# Revit family: equip-water-cooler-hlsy-tylr-oval2-ebp
name_source: partatom
category: Plumbing Fixtures
units: mm (PartAtom-declared; Revit-internal decimal feet)

## family parameters
Always vertical = Yes
Cut with Voids When Loaded = No
OmniClass Number = 23.45.00.00
OmniClass Title = Sanitary, Laundry, and Cleaning Equipment
Part Type = Normal
Room Calculation Point = No
Round Connector Dimension = Use Diameter
Shared = No
Work Plane-Based = No

## types (5) — shared parameters
Activation = Curved Pushbars
Apparent Load Phase 1 = 0 VA
Back Panel = Yes
Bubbler = Double Bubbler
CW Connection = Yes
Chiller Option = No
Cooler Depth = 1' - 6"
Cooler Width = 1' - 7 3/4"
Description = Water Cooler
Filter = **ACC (HWF172)
HW Connection = No
Left Hand Unit = No
Manufacturer = halseytaylor
Model = OVL-II EBP FTN
Mounting Plate = Incl Suface Mtg Plate
Number of Poles = 1
Right Hand Unit = Yes
Rim Height = 2' - 10"
Sanitary Service Size Radius = 0' - 0"
Specification URL = http://www.halseytaylor.com
Type = Single-Extended
URL = http://www.halseytaylor.com
Vent Connection = No
Version = 1.0.0.0
Voltage = 0 V
Volts/Hertz = 115V/60Hz
Waste Connection = Yes
Water Service Flow = 0 GPM
Water Service Flow Out = 0 GPM
Water Service Radius = 0' - 0"
Water Service Size Radius = 0' - 0 1/4"
zero-valued in all types: Power Factor

## per-type parameters (varying)
| type | Basin Material | Body Material | Bubbler Material | Freeze Resistant | Panel Material | Wall Plate Material |
| OVL-II EBP FTN SS | Metal - Steel - Stainless - Chrome | Metal - Steel - Stainless - Color 1 | Metal - Steel - Stainless - Chrome | See 7634008683 | Metal - Steel - Stainless - Chrome | Metal - Steel - Stainless - Chrome |
| OVL-II EBP FTN AG | Metal - Steel - Stainless - Aztec Gold | Metal - Steel - Stainless - Aztec Gold | Metal - Steel - Stainless - Aztec Gold |  | Metal - Steel - Stainless - Aztec Gold | Metal - Steel - Stainless - Aztec Gold |
| OVL-II EBP FTN AG/BO | Metal - Steel - Stainless - Onyx Black | Metal - Steel - Stainless - Aztec Gold | Metal - Steel - Stainless - Aztec Gold |  | Metal - Steel - Stainless - Aztec Gold | Metal - Steel - Stainless - Aztec Gold |
| OVL-II EBP FTN SS/BO | Metal - Steel - Stainless - Onyx Black | Metal - Steel - Stainless - Chrome | Metal - Steel - Stainless - Chrome |  | Metal - Steel - Stainless - Chrome | Metal - Steel - Stainless - Chrome |
| OVL-II EBP FTN SS/GG | Metal - Steel - Stainless - Color 1 | Metal - Steel - Stainless - Chrome | Metal - Steel - Stainless - Chrome |  | Metal - Steel - Stainless - Chrome | Metal - Steel - Stainless - Chrome |

## geometry (parser evidence)
native form markers: Sweep x5
no freeform markers — native parametric forms only
